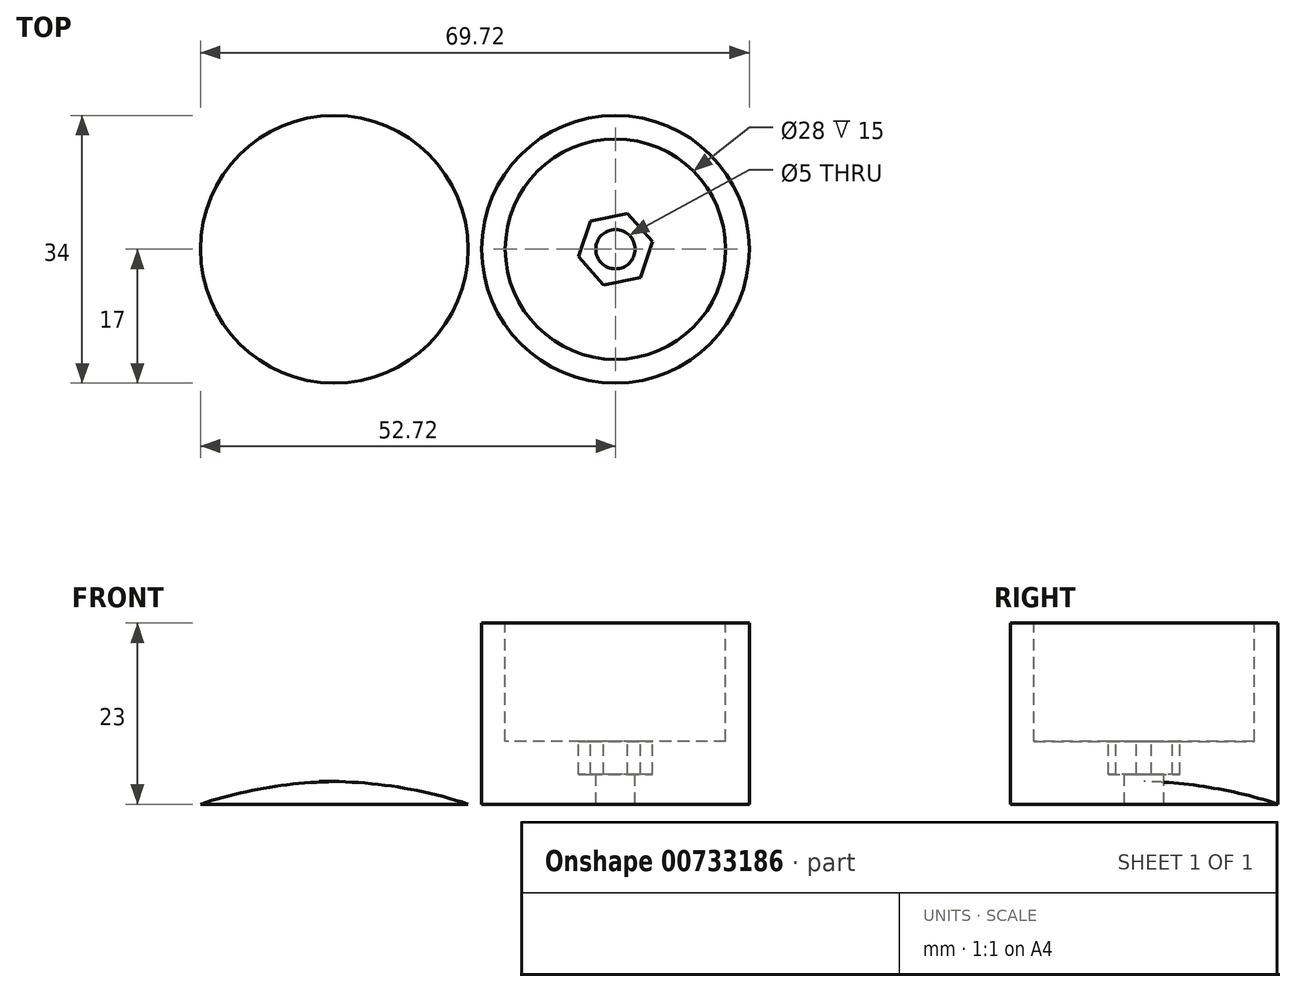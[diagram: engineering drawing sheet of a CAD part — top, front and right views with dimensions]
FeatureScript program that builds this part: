
annotation { "Feature Type Name" : "Feature", "Feature Type Description" : "" }
export const myFeature = defineFeature(function(context is Context, id is Id, definition is map)
    precondition{}
    {
        {
            var Q0;
            Q0=qCreatedBy(makeId("Top.planeOp"),FACE);
            var sketch = newSketch(context, id + "F0", { "sketchPlane" : qUnion([Q0])});
            skCircle(sketch, "E0", {"center": v(0, 0) * mm, "radius": 17 * mm});
            skSolve(sketch);
        }
        {
            var Q0;
            Q0=makeQuery(id+"F0.imprint","IMPRINT",FACE,{"disambiguationData":[TD([[makeQuery(id+"F0.imprint","IMPRINT",EDGE,{"derivedFrom":sQuery(id+"F0.wireOp",EDGE,"E0")}),1.0]])]});
            extrude(context, id + "F1", {"entities" : qUnion([Q0]), "depth" : 23 * mm, "offsetDistance" : 25 * mm});
        }
        {
            var Q0;
            Q0=makeQuery(id+"F1.opExtrude","CAP_FACE",FACE,{"disambiguationData":[OSD([sQuery(id+"F0.wireOp",EDGE,"E0")])],"isStart":false});
            var sketch = newSketch(context, id + "F2", { "sketchPlane" : qUnion([Q0])});
            skCircle(sketch, "E1", {"center": v(0, 0) * mm, "radius": 14 * mm});
            skSolve(sketch);
        }
        {
            var Q0;
            Q0 = qSketchRegion(id + "F2", true);
            extrude(context, id + "F3", {"entities" : qUnion([Q0]), "operationType" : NewBodyOperationType.REMOVE, "oppositeDirection" : true, "depth" : 15 * mm, "offsetDistance" : 25 * mm});
        }
        {
            var Q0;
            Q0=makeQuery(id+"F3.boolean.opBoolean","COPY",FACE,{"derivedFrom":makeQuery(id+"F3.opExtrude","CAP_FACE",FACE,{"disambiguationData":[OSD([sQuery(id+"F2.wireOp",EDGE,"E1")])],"isStart":false})});
            var sketch = newSketch(context, id + "F4", { "sketchPlane" : qUnion([Q0])});
            skCircle(sketch, "E2.cCircle", {"center": v(0, 0) * mm, "radius": 4.15 * mm, "construction": true});
            skLineSegment(sketch, "E2.0", {"start": v(4.7, 0.96) * mm, "end": v(3.18, -3.59) * mm});
            skLineSegment(sketch, "E2.1", {"start": v(3.18, -3.59) * mm, "end": v(-1.52, -4.55) * mm});
            skLineSegment(sketch, "E2.2", {"start": v(-1.52, -4.55) * mm, "end": v(-4.7, -0.96) * mm});
            skLineSegment(sketch, "E2.3", {"start": v(-4.7, -0.96) * mm, "end": v(-3.18, 3.59) * mm});
            skLineSegment(sketch, "E2.4", {"start": v(-3.18, 3.59) * mm, "end": v(1.52, 4.55) * mm});
            skLineSegment(sketch, "E2.5", {"start": v(1.52, 4.55) * mm, "end": v(4.7, 0.96) * mm});
            skPoint(sketch, "E2.0.midPoint", {"position": v(3.94, -1.31) * mm});
            skSolve(sketch);
        }
        {
            var Q0;
            Q0 = qSketchRegion(id + "F4", true);
            extrude(context, id + "F5", {"entities" : qUnion([Q0]), "operationType" : NewBodyOperationType.REMOVE, "oppositeDirection" : true, "depth" : 4.2 * mm, "offsetDistance" : 25 * mm});
        }
        {
            var Q0;
            Q0=makeQuery(id+"F5.boolean.opBoolean","COPY",FACE,{"derivedFrom":makeQuery(id+"F5.opExtrude","CAP_FACE",FACE,{"disambiguationData":[OSD([sQuery(id+"F4.wireOp",EDGE,"E2.0"),sQuery(id+"F4.wireOp",EDGE,"E2.1"),sQuery(id+"F4.wireOp",EDGE,"E2.2"),sQuery(id+"F4.wireOp",EDGE,"E2.3"),sQuery(id+"F4.wireOp",EDGE,"E2.4"),sQuery(id+"F4.wireOp",EDGE,"E2.5")])],"isStart":false})});
            var sketch = newSketch(context, id + "F6", { "sketchPlane" : qUnion([Q0])});
            skCircle(sketch, "E3", {"center": v(0, 0) * mm, "radius": 2.5 * mm});
            skSolve(sketch);
        }
        {
            var Q0;
            Q0 = qSketchRegion(id + "F6", true);
            extrude(context, id + "F7", {"entities" : qUnion([Q0]), "operationType" : NewBodyOperationType.REMOVE, "oppositeDirection" : true, "depth" : 25 * mm, "offsetDistance" : 25 * mm});
        }
        {
            var Q0;
            Q0=qCreatedBy(makeId("Front.planeOp"),FACE);
            var sketch = newSketch(context, id + "F8", { "sketchPlane" : qUnion([Q0])});
            skLineSegment(sketch, "E4", {"start": v(-35.72, 0) * mm, "end": v(-35.72, 19.79) * mm, "construction": true});
            skLineSegment(sketch, "E5", {"start": v(-35.72, 0) * mm, "end": v(-35.72, 2.87) * mm});
            skLineSegment(sketch, "E6", {"start": v(-35.72, 0) * mm, "end": v(-52.72, 0) * mm});
            skArc(sketch, "E7", {"start": v(-35.72, 2.87) * mm, "mid": v(-44.33, 2.08) * mm, "end": v(-52.72, 0) * mm});
            skPoint(sketch, "E7.third.point", {"position": v(-16.8, 0) * mm});
            skSolve(sketch);
        }
        {
            var Q0;
            Q0=makeQuery(id+"F8.imprint","IMPRINT",FACE,{"disambiguationData":[TD([[makeQuery(id+"F8.imprint","IMPRINT",EDGE,{"derivedFrom":sQuery(id+"F8.wireOp",EDGE,"E5")}),1.0]])]});
            var Q1;
            Q1=sQuery(id+"F8.wireOp",EDGE,"E4");
            revolve(context, id + "F9", {"surfaceOperationType" : NewSurfaceOperationType.NEW, "entities" : qUnion([Q0]), "axis" : qUnion([Q1]), "revolveType" : RevolveType.FULL});
        }
    });
